# Revit family: 307_Cim721-_
name_source: partatom
category: Pipe Accessories
units: mm (PartAtom-declared; Revit-internal decimal feet)

## family parameters
Always vertical = Yes
Cut with Voids When Loaded = No
Part Type = Breaks Into
Round Connector Dimension = Use Diameter
Shared = No
Work Plane-Based = No

## types (11) — shared parameters
CAT0 = Yes
D2 = 11 mm  [stored 0.0360892 ft]
Description = METERING STATION - PN 20 - "CR" BRASS
L1 = 16 mm  [stored 0.0524934 ft]
L1__ve = -16 mm  [stored -0.0524934 ft]
L2D_Min = 3048 mm
Manufacturer = Cimberio
QmdConnectorList = 301;D;302;D
URL = www.cimberio.it
magiPartTypeId = 307
magiProductFamilyId = Cim721-*
zero-valued in all types: MC_Default_elevation

## per-type parameters (varying)
| type | CenSd_R1_6 | D | H | H__ve | L2D | LL1 | LL2 | LL3 | R | R1 | W2D |
| Cim721L-15 | 12 mm  [stored 0.0393701 ft] | 15 mm | 58 mm  [stored 0.190289 ft] | -58 mm  [stored -0.190289 ft] | 67 mm | 34 mm | 51 mm  [stored 0.167323 ft] | 22 mm | 8 mm  [stored 0.0262467 ft] | 14 mm  [stored 0.0459318 ft] | 15 mm  [stored 0.0492126 ft] |
| Cim721-50 | 31 mm | 50 mm | 78 mm | -78 mm  [stored -0.255906 ft] | 80 mm | 40 mm  [stored 0.131234 ft] | 64 mm  [stored 0.209974 ft] | 24 mm  [stored 0.0787402 ft] | 25 mm  [stored 0.082021 ft] | 36 mm | 50 mm  [stored 0.164042 ft] |
| Cim721-40 | 24 mm  [stored 0.0787402 ft] | 40 mm | 72 mm | -72 mm  [stored -0.23622 ft] | 71 mm | 36 mm | 55 mm  [stored 0.180446 ft] | 23 mm | 20 mm  [stored 0.0656168 ft] | 28 mm  [stored 0.0918635 ft] | 40 mm  [stored 0.131234 ft] |
| Cim721-32 | 22 mm | 32 mm | 70 mm  [stored 0.229659 ft] | -70 mm  [stored -0.229659 ft] | 71 mm | 36 mm | 55 mm  [stored 0.180446 ft] | 23 mm | 16 mm  [stored 0.0524934 ft] | 26 mm | 32 mm  [stored 0.104987 ft] |
| Cim721-25 | 17 mm  [stored 0.0557743 ft] | 25 mm | 64 mm  [stored 0.209974 ft] | -64 mm  [stored -0.209974 ft] | 64 mm  [stored 0.209974 ft] | 32 mm  [stored 0.104987 ft] | 48 mm  [stored 0.15748 ft] | 21 mm | 13 mm | 20 mm  [stored 0.0656168 ft] | 25 mm  [stored 0.082021 ft] |
| Cim721-20 | 15 mm  [stored 0.0492126 ft] | 20 mm | 62 mm  [stored 0.203412 ft] | -62 mm  [stored -0.203412 ft] | 67 mm | 34 mm | 51 mm  [stored 0.167323 ft] | 22 mm | 10 mm  [stored 0.0328084 ft] | 17 mm  [stored 0.0557743 ft] | 20 mm  [stored 0.0656168 ft] |
| Cim721-15 | 12 mm  [stored 0.0393701 ft] | 15 mm | 58 mm  [stored 0.190289 ft] | -58 mm  [stored -0.190289 ft] | 67 mm | 34 mm | 51 mm  [stored 0.167323 ft] | 22 mm | 8 mm  [stored 0.0262467 ft] | 14 mm  [stored 0.0459318 ft] | 15 mm  [stored 0.0492126 ft] |
| Cim721UUL-15 | 12 mm  [stored 0.0393701 ft] | 15 mm | 58 mm  [stored 0.190289 ft] | -58 mm  [stored -0.190289 ft] | 67 mm | 34 mm | 51 mm  [stored 0.167323 ft] | 22 mm | 8 mm  [stored 0.0262467 ft] | 14 mm  [stored 0.0459318 ft] | 15 mm  [stored 0.0492126 ft] |
| Cim721ULL-15 | 12 mm  [stored 0.0393701 ft] | 15 mm | 58 mm  [stored 0.190289 ft] | -58 mm  [stored -0.190289 ft] | 67 mm | 34 mm | 51 mm  [stored 0.167323 ft] | 22 mm | 8 mm  [stored 0.0262467 ft] | 14 mm  [stored 0.0459318 ft] | 15 mm  [stored 0.0492126 ft] |
| Cim721UL-15 | 12 mm  [stored 0.0393701 ft] | 15 mm | 58 mm  [stored 0.190289 ft] | -58 mm  [stored -0.190289 ft] | 67 mm | 34 mm | 51 mm  [stored 0.167323 ft] | 22 mm | 8 mm  [stored 0.0262467 ft] | 14 mm  [stored 0.0459318 ft] | 15 mm  [stored 0.0492126 ft] |
| Cim721M-15 | 12 mm  [stored 0.0393701 ft] | 15 mm | 58 mm  [stored 0.190289 ft] | -58 mm  [stored -0.190289 ft] | 67 mm | 34 mm | 51 mm  [stored 0.167323 ft] | 22 mm | 8 mm  [stored 0.0262467 ft] | 14 mm  [stored 0.0459318 ft] | 15 mm  [stored 0.0492126 ft] |

note: column(s) folded — value = type name in every type: magiProductCode, magiProductId

note: [stored X ft] marks values corroborated as IEEE doubles in the binary element streams (Revit-internal decimal feet)

## geometry (parser evidence)
native form markers: Sweep x2
no freeform markers — native parametric forms only
